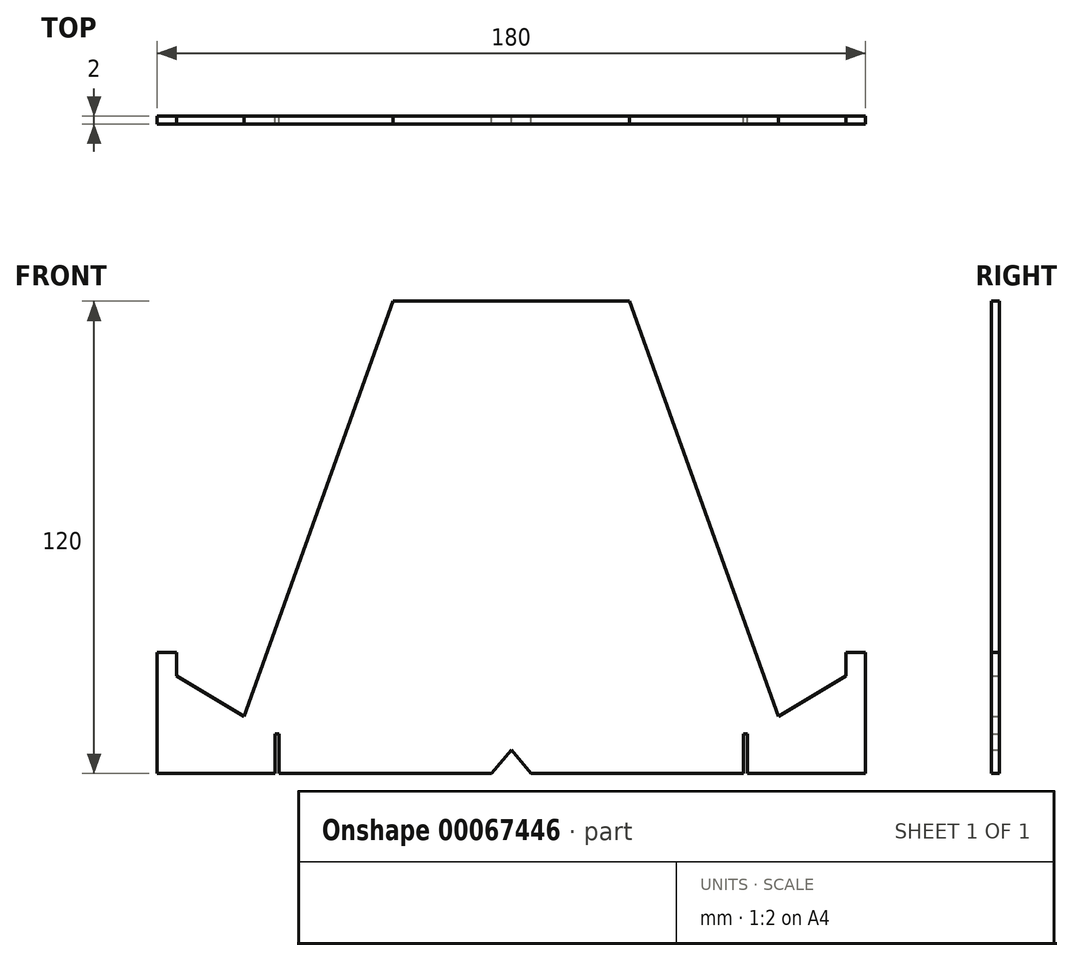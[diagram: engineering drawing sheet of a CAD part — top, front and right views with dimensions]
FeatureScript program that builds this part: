
annotation { "Feature Type Name" : "Feature", "Feature Type Description" : "" }
export const myFeature = defineFeature(function(context is Context, id is Id, definition is map)
    precondition{}
    {
        {
            var Q0;
            Q0=qCreatedBy(makeId("Front.planeOp"),FACE);
            var sketch = newSketch(context, id + "F0", { "sketchPlane" : qUnion([Q0])});
            skLineSegment(sketch, "E0.bottom", {"start": v(-33.7, 85.35) * mm, "end": v(26.3, 85.35) * mm});
            skLineSegment(sketch, "E0.top", {"start": v(-93.7, -34.65) * mm, "end": v(-63.7, -34.65) * mm});
            skLineSegment(sketch, "E0.left", {"start": v(-93.7, -3.87) * mm, "end": v(-93.7, -34.65) * mm});
            skLineSegment(sketch, "E0.right", {"start": v(86.3, -3.87) * mm, "end": v(86.3, -34.65) * mm});
            skLineSegment(sketch, "E1.top", {"start": v(56.3, -24.65) * mm, "end": v(55.3, -24.65) * mm});
            skLineSegment(sketch, "E1.left", {"start": v(56.3, -34.65) * mm, "end": v(56.3, -24.65) * mm});
            skLineSegment(sketch, "E1.right", {"start": v(55.3, -34.65) * mm, "end": v(55.3, -24.65) * mm});
            skLineSegment(sketch, "E2.top", {"start": v(-63.7, -24.65) * mm, "end": v(-62.7, -24.65) * mm});
            skLineSegment(sketch, "E2.left", {"start": v(-63.7, -34.65) * mm, "end": v(-63.7, -24.65) * mm});
            skLineSegment(sketch, "E2.right", {"start": v(-62.7, -34.65) * mm, "end": v(-62.7, -24.65) * mm});
            skLineSegment(sketch, "E3.bottom", {"start": v(-23.7, 85.35) * mm, "end": v(16.3, 85.35) * mm});
            skLineSegment(sketch, "E3.top", {"start": v(-23.7, -34.65) * mm, "end": v(-8.7, -34.65) * mm});
            skLineSegment(sketch, "E3.left", {"start": v(-23.7, 85.35) * mm, "end": v(-23.7, -34.65) * mm});
            skLineSegment(sketch, "E3.right", {"start": v(16.3, 85.35) * mm, "end": v(16.3, -34.65) * mm});
            skPoint(sketch, "E4", {"position": v(-8.7, -34.65) * mm});
            skPoint(sketch, "E5", {"position": v(-3.7, -28.65) * mm});
            skPoint(sketch, "E6", {"position": v(1.3, -34.65) * mm});
            skLineSegment(sketch, "E7", {"start": v(-3.7, -28.65) * mm, "end": v(-8.7, -34.65) * mm});
            skLineSegment(sketch, "E8", {"start": v(-3.7, -28.65) * mm, "end": v(1.3, -34.65) * mm});
            skLineSegment(sketch, "E9.trimOffspring", {"start": v(1.3, -34.65) * mm, "end": v(55.3, -34.65) * mm});
            skLineSegment(sketch, "E10.trimOffspring", {"start": v(1.3, -34.65) * mm, "end": v(16.3, -34.65) * mm});
            skLineSegment(sketch, "E11.top", {"start": v(86.3, -34.65) * mm, "end": v(81.3, -34.65) * mm});
            skLineSegment(sketch, "E11.left", {"start": v(86.3, -4.65) * mm, "end": v(86.3, -34.65) * mm});
            skLineSegment(sketch, "E12", {"start": v(26.3, 85.35) * mm, "end": v(64.14, -20.21) * mm});
            skLineSegment(sketch, "E13", {"start": v(64.14, -20.21) * mm, "end": v(81.3, -9.93) * mm});
            skLineSegment(sketch, "E14", {"start": v(81.3, -9.93) * mm, "end": v(81.3, -3.87) * mm});
            skLineSegment(sketch, "E15", {"start": v(81.3, -3.87) * mm, "end": v(86.3, -3.87) * mm});
            skLineSegment(sketch, "E16", {"start": v(-3.7, 85.35) * mm, "end": v(-3.7, -28.65) * mm, "construction": true});
            skLineSegment(sketch, "E17.MirrorCS", {"start": v(-33.7, 85.35) * mm, "end": v(-71.55, -20.21) * mm});
            skLineSegment(sketch, "E18.MirrorCS", {"start": v(-71.55, -20.21) * mm, "end": v(-88.7, -9.93) * mm});
            skLineSegment(sketch, "E19.MirrorCS", {"start": v(-88.7, -9.93) * mm, "end": v(-88.7, -3.87) * mm});
            skLineSegment(sketch, "E20.MirrorCS", {"start": v(-88.7, -3.87) * mm, "end": v(-93.7, -3.87) * mm});
            skLineSegment(sketch, "E21.trimOffspring", {"start": v(56.3, -34.65) * mm, "end": v(86.3, -34.65) * mm});
            skLineSegment(sketch, "E22.trimOffspring", {"start": v(-62.7, -34.65) * mm, "end": v(-8.7, -34.65) * mm});
            skSolve(sketch);
        }
        {
            var Q0;
            Q0 = qSketchRegion(id + "F0", true);
            extrude(context, id + "F1", {"entities" : qUnion([Q0]), "depth" : 2 * mm});
        }
    });
